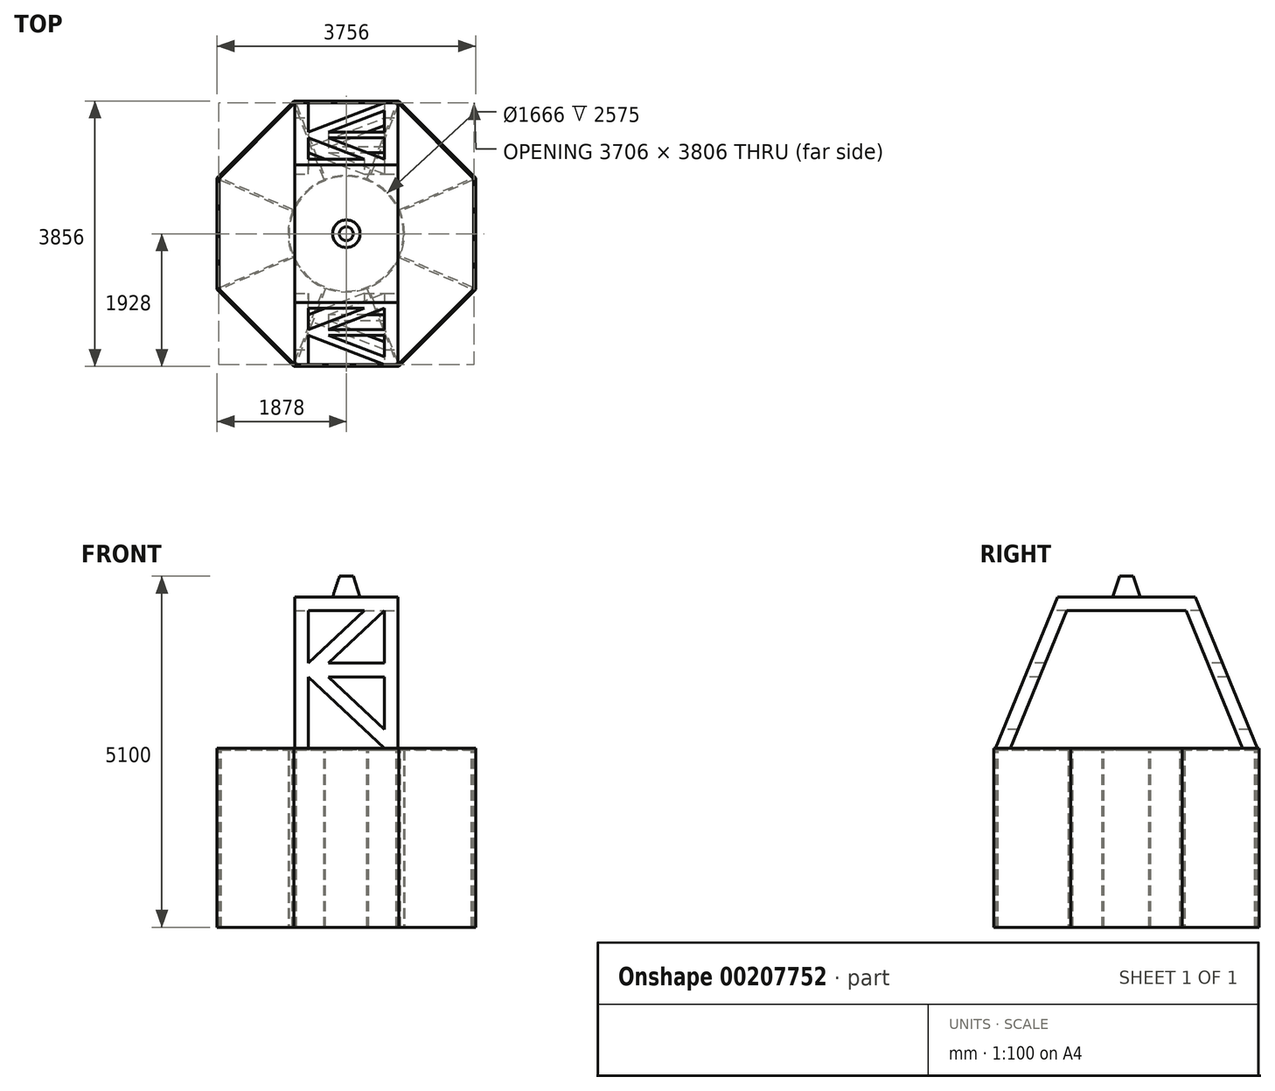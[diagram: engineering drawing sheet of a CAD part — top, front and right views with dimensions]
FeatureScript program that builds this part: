
annotation { "Feature Type Name" : "Feature", "Feature Type Description" : "" }
export const myFeature = defineFeature(function(context is Context, id is Id, definition is map)
    precondition{}
    {
        {
            var Q0;
            Q0=qCreatedBy(makeId("Top.planeOp"),FACE);
            cPlane(context, id + "F0", {"entities" : qUnion([Q0]), "cplaneType" : CPlaneType.OFFSET, "offset" : 4071 * mm, "width" : 150 * mm, "height" : 150 * mm});
        }
        {
            var Q0;
            Q0=qCreatedBy(id+"F0.planeOp",FACE);
            var sketch = newSketch(context, id + "F1", { "sketchPlane" : qUnion([Q0])});
            skCircle(sketch, "E0", {"center": v(0, 0) * mm, "radius": 833 * mm});
            skCircle(sketch, "E1", {"center": v(0, 0) * mm, "radius": 845.7 * mm});
            skSolve(sketch);
        }
        {
            var Q0;
            Q0 = qSketchRegion(id + "F1", true);
            extrude(context, id + "F2", {"entities" : qUnion([Q0]), "depth" : 2600 * mm, "offsetDistance" : 25 * mm});
        }
        {
            var Q0;
            Q0=makeQuery(id+"F2.opExtrude","CAP_FACE",FACE,{"disambiguationData":[OSD([sQuery(id+"F1.wireOp",EDGE,"E0"),sQuery(id+"F1.wireOp",EDGE,"E1")])],"isStart":false});
            var sketch = newSketch(context, id + "F3", { "sketchPlane" : qUnion([Q0])});
            skLineSegment(sketch, "E2", {"start": v(0, 0) * mm, "end": v(0, 2211.58) * mm, "construction": true});
            skLineSegment(sketch, "E3", {"start": v(0, 0) * mm, "end": v(2373.76, 0) * mm, "construction": true});
            skLineSegment(sketch, "E4", {"start": v(750, 1900) * mm, "end": v(-750, 1900) * mm});
            skLineSegment(sketch, "E5", {"start": v(-750, 1900) * mm, "end": v(-1850, 800) * mm});
            skLineSegment(sketch, "E6", {"start": v(-1850, 800) * mm, "end": v(-1850, -800) * mm});
            skLineSegment(sketch, "E7", {"start": v(-1850, -800) * mm, "end": v(-750, -1900) * mm});
            skLineSegment(sketch, "E8", {"start": v(-750, -1900) * mm, "end": v(750, -1900) * mm});
            skLineSegment(sketch, "E9", {"start": v(750, -1900) * mm, "end": v(1850, -800) * mm});
            skLineSegment(sketch, "E10", {"start": v(1850, -800) * mm, "end": v(1850, 800) * mm});
            skLineSegment(sketch, "E11", {"start": v(1850, 800) * mm, "end": v(750, 1900) * mm});
            skSolve(sketch);
        }
        {
            var Q0;
            Q0 = qSketchRegion(id + "F3", true);
            extrude(context, id + "F4", {"entities" : qUnion([Q0]), "operationType" : NewBodyOperationType.ADD, "oppositeDirection" : true, "depth" : 25 * mm, "offsetDistance" : 25 * mm});
        }
        {
            var Q0;
            Q0=makeQuery(id+"F4.boolean.opBoolean","MERGE",FACE,{"derivedFrom":[makeQuery(id+"F2.opExtrude","CAP_FACE",FACE,{"disambiguationData":[OSD([sQuery(id+"F1.wireOp",EDGE,"E0"),sQuery(id+"F1.wireOp",EDGE,"E1")])],"isStart":false}),makeQuery(id+"F4.opExtrude","CAP_FACE",FACE,{"disambiguationData":[OSD([sQuery(id+"F3.wireOp",EDGE,"E4"),sQuery(id+"F3.wireOp",EDGE,"E5"),sQuery(id+"F3.wireOp",EDGE,"E6"),sQuery(id+"F3.wireOp",EDGE,"E7"),sQuery(id+"F3.wireOp",EDGE,"E8"),sQuery(id+"F3.wireOp",EDGE,"E9"),sQuery(id+"F3.wireOp",EDGE,"E10"),sQuery(id+"F3.wireOp",EDGE,"E11")])],"isStart":true})]});
            var sketch = newSketch(context, id + "F5", { "sketchPlane" : qUnion([Q0])});
            skLineSegment(sketch, "E12", {"start": v(-750, -1900) * mm, "end": v(750, 1900) * mm, "construction": true});
            skLineSegment(sketch, "E13", {"start": v(-750, 1900) * mm, "end": v(750, -1900) * mm, "construction": true});
            skLineSegment(sketch, "E14", {"start": v(-1850, 800) * mm, "end": v(1850, -800) * mm, "construction": true});
            skLineSegment(sketch, "E15", {"start": v(-1850, -800) * mm, "end": v(1850, 800) * mm, "construction": true});
            skLineSegment(sketch, "E16", {"start": v(-1818.5, 800) * mm, "end": v(-1828.43, 777.05) * mm});
            skLineSegment(sketch, "E17", {"start": v(-1828.43, 777.05) * mm, "end": v(-788.54, 327.37) * mm});
            skLineSegment(sketch, "E18", {"start": v(-788.54, 327.37) * mm, "end": v(-778.61, 350.32) * mm});
            skLineSegment(sketch, "E19", {"start": v(-778.61, 350.32) * mm, "end": v(-1818.5, 800) * mm});
            skLineSegment(sketch, "E20", {"start": v(-750, 1865.96) * mm, "end": v(-726.75, 1875.13) * mm});
            skLineSegment(sketch, "E21", {"start": v(-726.75, 1875.13) * mm, "end": v(-301.86, 798.75) * mm});
            skLineSegment(sketch, "E22", {"start": v(-301.86, 798.75) * mm, "end": v(-325.1, 789.57) * mm});
            skLineSegment(sketch, "E23", {"start": v(-325.1, 789.57) * mm, "end": v(-750, 1865.96) * mm});
            skLineSegment(sketch, "E24", {"start": v(726.44, 1875.13) * mm, "end": v(749.92, 1864.98) * mm});
            skLineSegment(sketch, "E25", {"start": v(749.92, 1864.98) * mm, "end": v(325.35, 789.4) * mm});
            skLineSegment(sketch, "E26", {"start": v(325.35, 789.4) * mm, "end": v(301.56, 798.78) * mm});
            skLineSegment(sketch, "E27", {"start": v(301.56, 798.78) * mm, "end": v(726.44, 1875.13) * mm});
            skLineSegment(sketch, "E28", {"start": v(1817.76, 800) * mm, "end": v(1827.92, 776.51) * mm});
            skLineSegment(sketch, "E29", {"start": v(1827.92, 776.51) * mm, "end": v(788.03, 326.83) * mm});
            skLineSegment(sketch, "E30", {"start": v(788.03, 326.83) * mm, "end": v(777.87, 350.32) * mm});
            skLineSegment(sketch, "E31", {"start": v(777.87, 350.32) * mm, "end": v(1817.76, 800) * mm});
            skLineSegment(sketch, "E32", {"start": v(788.55, -327.06) * mm, "end": v(779.15, -350.87) * mm});
            skLineSegment(sketch, "E33", {"start": v(779.15, -350.87) * mm, "end": v(1817.76, -800) * mm});
            skLineSegment(sketch, "E34", {"start": v(1817.76, -800) * mm, "end": v(1827.92, -776.51) * mm});
            skLineSegment(sketch, "E35", {"start": v(1827.92, -776.51) * mm, "end": v(788.55, -327.06) * mm});
            skLineSegment(sketch, "E36", {"start": v(325.35, -789.38) * mm, "end": v(301.55, -798.77) * mm});
            skLineSegment(sketch, "E37", {"start": v(301.55, -798.77) * mm, "end": v(726.5, -1875.33) * mm});
            skLineSegment(sketch, "E38", {"start": v(726.5, -1875.33) * mm, "end": v(750.3, -1865.93) * mm});
            skLineSegment(sketch, "E39", {"start": v(750.3, -1865.93) * mm, "end": v(325.35, -789.38) * mm});
            skLineSegment(sketch, "E40", {"start": v(-325.34, -789.38) * mm, "end": v(-301.86, -799.53) * mm});
            skLineSegment(sketch, "E41", {"start": v(-301.86, -799.53) * mm, "end": v(-726.51, -1875.33) * mm});
            skLineSegment(sketch, "E42", {"start": v(-726.51, -1875.33) * mm, "end": v(-750, -1865.17) * mm});
            skLineSegment(sketch, "E43", {"start": v(-750, -1865.17) * mm, "end": v(-325.34, -789.38) * mm});
            skLineSegment(sketch, "E44", {"start": v(-788.54, -327.06) * mm, "end": v(-778.38, -350.53) * mm});
            skLineSegment(sketch, "E45", {"start": v(-778.38, -350.53) * mm, "end": v(-1818.5, -800.31) * mm});
            skLineSegment(sketch, "E46", {"start": v(-1818.5, -800.31) * mm, "end": v(-1827.9, -776.51) * mm});
            skLineSegment(sketch, "E47", {"start": v(-1827.9, -776.51) * mm, "end": v(-788.54, -327.06) * mm});
            skSolve(sketch);
        }
        {
            var Q0;
            Q0 = qSketchRegion(id + "F5", true);
            var Q1;
            Q1=makeQuery(id+"F2.opExtrude","CAP_FACE",FACE,{"disambiguationData":[OSD([sQuery(id+"F1.wireOp",EDGE,"E0"),sQuery(id+"F1.wireOp",EDGE,"E1")])],"isStart":true});
            extrude(context, id + "F6", {"entities" : qUnion([Q0]), "operationType" : NewBodyOperationType.ADD, "endBound" : BoundingType.UP_TO_SURFACE, "oppositeDirection" : true, "depth" : 25 * mm, "endBoundEntityFace" : qUnion([Q1]), "offsetDistance" : 25 * mm});
        }
        {
            var Q0;
            Q0=makeQuery(id+"F4.boolean.opBoolean","MERGE",FACE,{"derivedFrom":[makeQuery(id+"F2.opExtrude","CAP_FACE",FACE,{"disambiguationData":[OSD([sQuery(id+"F1.wireOp",EDGE,"E0"),sQuery(id+"F1.wireOp",EDGE,"E1")])],"isStart":false}),makeQuery(id+"F4.opExtrude","CAP_FACE",FACE,{"disambiguationData":[OSD([sQuery(id+"F3.wireOp",EDGE,"E4"),sQuery(id+"F3.wireOp",EDGE,"E5"),sQuery(id+"F3.wireOp",EDGE,"E6"),sQuery(id+"F3.wireOp",EDGE,"E7"),sQuery(id+"F3.wireOp",EDGE,"E8"),sQuery(id+"F3.wireOp",EDGE,"E9"),sQuery(id+"F3.wireOp",EDGE,"E10"),sQuery(id+"F3.wireOp",EDGE,"E11")])],"isStart":true})]});
            var sketch = newSketch(context, id + "F7", { "sketchPlane" : qUnion([Q0])});
            skLineSegment(sketch, "E48", {"start": v(-1850, 800) * mm, "end": v(1850, -800) * mm, "construction": true});
            skLineSegment(sketch, "E49", {"start": v(-750, 1900) * mm, "end": v(750, -1900) * mm, "construction": true});
            skLineSegment(sketch, "E50", {"start": v(750, 1900) * mm, "end": v(-750, -1900) * mm, "construction": true});
            skLineSegment(sketch, "E51", {"start": v(-1850, -800) * mm, "end": v(1850, 800) * mm, "construction": true});
            skPoint(sketch, "E52", {"position": v(-750, 1900) * mm});
            skPoint(sketch, "E53", {"position": v(750, 1900) * mm});
            skPoint(sketch, "E54", {"position": v(-1850, -800) * mm});
            skPoint(sketch, "E55", {"position": v(-750, -1900) * mm});
            skPoint(sketch, "E56", {"position": v(750, -1900) * mm});
            skPoint(sketch, "E57", {"position": v(1850, -800) * mm});
            skSolve(sketch);
        }
        {
            var Q0;
            Q0=makeQuery(id+"F7.imprint","IMPRINT",FACE,{"disambiguationData":[TD([[makeQuery(id+"F7.imprint","IMPRINT",EDGE,{"derivedFrom":makeQuery(id+"F4.opExtrude","CAP_EDGE",EDGE,{"disambiguationData":[OSD([sQuery(id+"F3.wireOp",EDGE,"E4")])],"isStart":true})}),1.0]])]});
            cPlane(context, id + "F8", {"entities" : qUnion([Q0]), "cplaneType" : CPlaneType.OFFSET, "offset" : 2200 * mm, "width" : 150 * mm, "height" : 150 * mm});
        }
        {
            var Q0;
            Q0=makeQuery(id+"F7.imprint","IMPRINT",FACE,{"disambiguationData":[TD([[makeQuery(id+"F7.imprint","IMPRINT",EDGE,{"derivedFrom":makeQuery(id+"F4.opExtrude","CAP_EDGE",EDGE,{"disambiguationData":[OSD([sQuery(id+"F3.wireOp",EDGE,"E4")])],"isStart":true})}),1.0]])]});
            var sketch = newSketch(context, id + "F9", { "sketchPlane" : qUnion([Q0])});
            skLineSegment(sketch, "E58.0", {"start": v(751.24, 1903) * mm, "end": v(-751.24, 1903) * mm});
            skLineSegment(sketch, "E58.1", {"start": v(1853, 801.24) * mm, "end": v(751.24, 1903) * mm});
            skLineSegment(sketch, "E58.2", {"start": v(-751.24, 1903) * mm, "end": v(-1853, 801.24) * mm});
            skLineSegment(sketch, "E58.3", {"start": v(1853, -801.24) * mm, "end": v(1853, 801.24) * mm});
            skLineSegment(sketch, "E58.4", {"start": v(-1853, 801.24) * mm, "end": v(-1853, -801.24) * mm});
            skLineSegment(sketch, "E58.5", {"start": v(-1853, -801.24) * mm, "end": v(-751.24, -1903) * mm});
            skLineSegment(sketch, "E58.6", {"start": v(-751.24, -1903) * mm, "end": v(751.24, -1903) * mm});
            skLineSegment(sketch, "E58.7", {"start": v(751.24, -1903) * mm, "end": v(1853, -801.24) * mm});
            skLineSegment(sketch, "E59.0", {"start": v(761.6, 1928) * mm, "end": v(-761.6, 1928) * mm});
            skLineSegment(sketch, "E59.1", {"start": v(1878, 811.6) * mm, "end": v(761.6, 1928) * mm});
            skLineSegment(sketch, "E59.2", {"start": v(-761.6, 1928) * mm, "end": v(-1878, 811.6) * mm});
            skLineSegment(sketch, "E59.3", {"start": v(1878, -811.6) * mm, "end": v(1878, 811.6) * mm});
            skLineSegment(sketch, "E59.4", {"start": v(-1878, 811.6) * mm, "end": v(-1878, -811.6) * mm});
            skLineSegment(sketch, "E59.5", {"start": v(-1878, -811.6) * mm, "end": v(-761.6, -1928) * mm});
            skLineSegment(sketch, "E59.6", {"start": v(-761.6, -1928) * mm, "end": v(761.6, -1928) * mm});
            skLineSegment(sketch, "E59.7", {"start": v(761.6, -1928) * mm, "end": v(1878, -811.6) * mm});
            skSolve(sketch);
        }
        {
            var Q0;
            Q0 = qSketchRegion(id + "F9", true);
            var Q1;
            Q1=makeQuery(id+"F6.opExtrude","CAP_FACE",FACE,{"disambiguationData":[OSD([sQuery(id+"F5.wireOp",EDGE,"E44"),sQuery(id+"F5.wireOp",EDGE,"E45"),sQuery(id+"F5.wireOp",EDGE,"E46"),sQuery(id+"F5.wireOp",EDGE,"E47")])],"isStart":false});
            extrude(context, id + "F10", {"entities" : qUnion([Q0]), "endBound" : BoundingType.UP_TO_SURFACE, "oppositeDirection" : true, "depth" : 25 * mm, "endBoundEntityFace" : qUnion([Q1]), "offsetDistance" : 25 * mm});
        }
        {
            var Q0;
            Q0=qCreatedBy(makeId("Right.planeOp"),FACE);
            var Q1;
            Q1=sQuery(id+"F7.wireOp",VERTEX,"E55");
            cPlane(context, id + "F11", {"entities" : qUnion([Q0, Q1]), "cplaneType" : CPlaneType.PLANE_POINT, "offset" : 25 * mm, "width" : 150 * mm, "height" : 150 * mm});
        }
        {
            var Q0;
            Q0=sQuery(id+"F7.wireOp",VERTEX,"E56");
            var Q1;
            Q1=qCreatedBy(makeId("Right.planeOp"),FACE);
            cPlane(context, id + "F12", {"entities" : qUnion([Q0, Q1]), "cplaneType" : CPlaneType.PLANE_POINT, "offset" : 25 * mm, "width" : 150 * mm, "height" : 150 * mm});
        }
        {
            var Q0;
            Q0=qCreatedBy(id+"F12.planeOp",FACE);
            var sketch = newSketch(context, id + "F13", { "sketchPlane" : qUnion([Q0])});
            skLineSegment(sketch, "E60", {"start": v(-1000, 8871) * mm, "end": v(-1900, 6671) * mm});
            skLineSegment(sketch, "E61", {"start": v(-1900, 6671) * mm, "end": v(-1683.91, 6671) * mm});
            skLineSegment(sketch, "E62", {"start": v(-1683.91, 6671) * mm, "end": v(-865.73, 8671) * mm});
            skLineSegment(sketch, "E63", {"start": v(-865.73, 8671) * mm, "end": v(865.73, 8671) * mm});
            skLineSegment(sketch, "E64", {"start": v(865.73, 8671) * mm, "end": v(1683.91, 6671) * mm});
            skLineSegment(sketch, "E65", {"start": v(1683.91, 6671) * mm, "end": v(1900, 6671) * mm});
            skLineSegment(sketch, "E66", {"start": v(1900, 6671) * mm, "end": v(1000, 8871) * mm});
            skLineSegment(sketch, "E67", {"start": v(1000, 8871) * mm, "end": v(-1000, 8871) * mm});
            skLineSegment(sketch, "E68", {"start": v(0, 0) * mm, "end": v(0, 2921.5) * mm, "construction": true});
            skSolve(sketch);
        }
        {
            var Q0;
            Q0 = qSketchRegion(id + "F13", true);
            var Q1;
            Q1=qCreatedBy(id+"F11.planeOp",FACE);
            extrude(context, id + "F14", {"entities" : qUnion([Q0]), "operationType" : NewBodyOperationType.ADD, "endBound" : BoundingType.UP_TO_SURFACE, "oppositeDirection" : true, "depth" : 25 * mm, "endBoundEntityFace" : qUnion([Q1]), "offsetDistance" : 25 * mm});
        }
        {
            var Q0;
            Q0=qCreatedBy(makeId("Front.planeOp"),FACE);
            var sketch = newSketch(context, id + "F15", { "sketchPlane" : qUnion([Q0])});
            skLineSegment(sketch, "E69", {"start": v(-550, 6671) * mm, "end": v(-550, 7708.46) * mm});
            skLineSegment(sketch, "E70", {"start": v(-550, 7708.46) * mm, "end": v(550, 6671) * mm});
            skLineSegment(sketch, "E71", {"start": v(550, 6671) * mm, "end": v(-550, 6671) * mm});
            skLineSegment(sketch, "E72", {"start": v(-258.5, 7708.46) * mm, "end": v(550, 6945.92) * mm});
            skLineSegment(sketch, "E73", {"start": v(550, 6945.92) * mm, "end": v(550, 7708.46) * mm});
            skLineSegment(sketch, "E74", {"start": v(550, 7708.46) * mm, "end": v(-258.5, 7708.46) * mm});
            skLineSegment(sketch, "E75", {"start": v(-258.5, 7908.46) * mm, "end": v(550, 7908.46) * mm});
            skLineSegment(sketch, "E76", {"start": v(550, 7908.46) * mm, "end": v(550, 8671) * mm});
            skLineSegment(sketch, "E77", {"start": v(550, 8671) * mm, "end": v(-258.5, 7908.46) * mm});
            skLineSegment(sketch, "E78", {"start": v(-550, 7908.46) * mm, "end": v(258.5, 8671) * mm});
            skLineSegment(sketch, "E79", {"start": v(258.5, 8671) * mm, "end": v(-550, 8671) * mm});
            skLineSegment(sketch, "E80", {"start": v(-550, 8671) * mm, "end": v(-550, 7908.46) * mm});
            skSolve(sketch);
        }
        {
            var Q0;
            Q0 = qSketchRegion(id + "F15", true);
            extrude(context, id + "F16", {"entities" : qUnion([Q0]), "operationType" : NewBodyOperationType.REMOVE, "endBound" : BoundingType.SYMMETRIC, "oppositeDirection" : true, "depth" : 5000 * mm, "offsetDistance" : 25 * mm});
        }
        {
            var Q0;
            Q0=qCreatedBy(makeId("Front.planeOp"),FACE);
            var sketch = newSketch(context, id + "F17", { "sketchPlane" : qUnion([Q0])});
            skLineSegment(sketch, "E81", {"start": v(0, 0) * mm, "end": v(0, 8871) * mm, "construction": true});
            skLineSegment(sketch, "E82", {"start": v(-100, 9171) * mm, "end": v(-200, 8871) * mm});
            skLineSegment(sketch, "E83", {"start": v(-200, 8871) * mm, "end": v(0, 8871) * mm});
            skLineSegment(sketch, "E84", {"start": v(0, 9171) * mm, "end": v(-100, 9171) * mm});
            skLineSegment(sketch, "E85", {"start": v(0, 9171) * mm, "end": v(0, 8871) * mm});
            skSolve(sketch);
        }
        {
            var Q0;
            Q0=makeQuery(id+"F17.imprint","IMPRINT",FACE,{"disambiguationData":[TD([[makeQuery(id+"F17.imprint","IMPRINT",EDGE,{"derivedFrom":sQuery(id+"F17.wireOp",EDGE,"E82")}),1.0]])]});
            var Q1;
            Q1=sQuery(id+"F17.wireOp",EDGE,"E81");
            revolve(context, id + "F18", {"operationType" : NewBodyOperationType.ADD, "surfaceOperationType" : NewSurfaceOperationType.NEW, "entities" : qUnion([Q0]), "axis" : qUnion([Q1]), "revolveType" : RevolveType.FULL});
        }
    });
